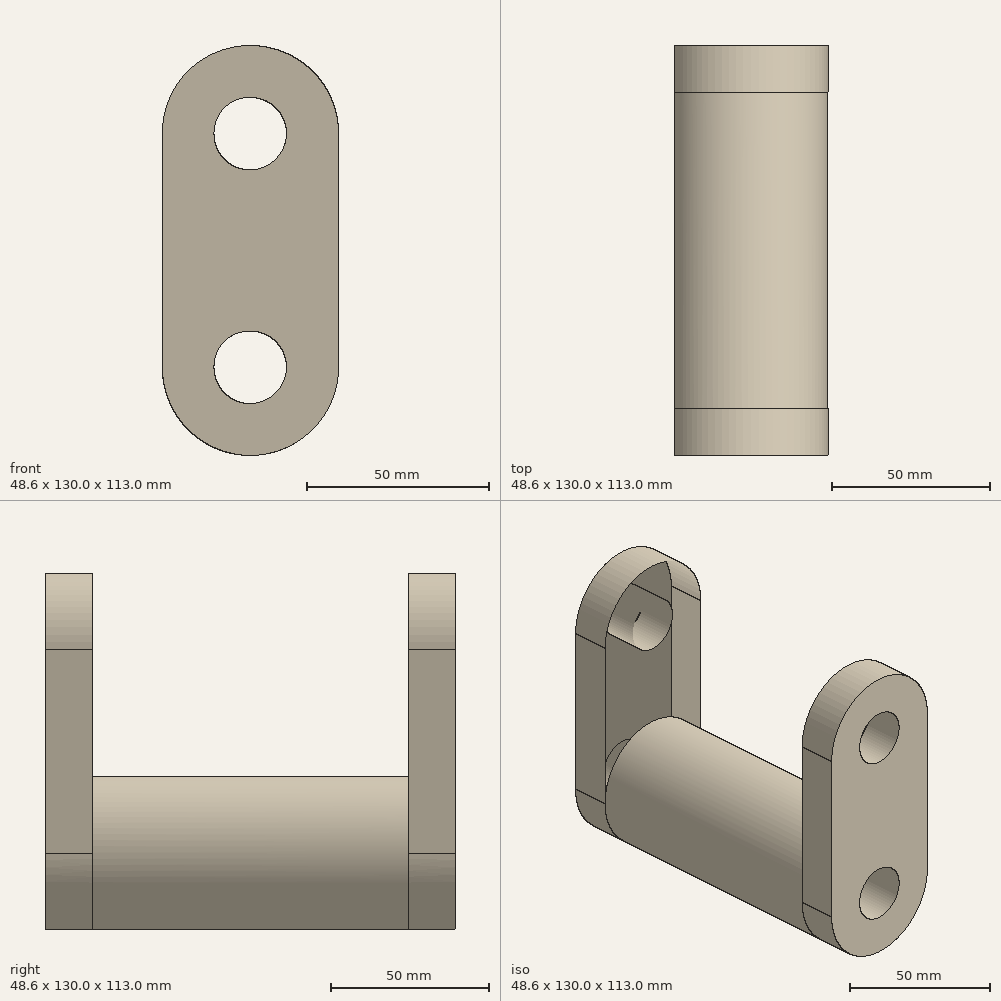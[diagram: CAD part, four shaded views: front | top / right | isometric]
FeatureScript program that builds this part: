
annotation { "Feature Type Name" : "Feature", "Feature Type Description" : "" }
export const myFeature = defineFeature(function(context is Context, id is Id, definition is map)
    precondition{}
    {
        {
            var Q0;
            Q0=qCreatedBy(makeId("Front.planeOp"),FACE);
            var sketch = newSketch(context, id + "F0", { "sketchPlane" : qUnion([Q0])});
            skCircle(sketch, "E0", {"center": v(0, -24.59) * mm, "radius": 24.22 * mm});
            skSolve(sketch);
        }
        {
            var Q0;
            Q0=makeQuery(id+"F0.imprint","IMPRINT",FACE,{"disambiguationData":[TD([[makeQuery(id+"F0.imprint","IMPRINT",EDGE,{"derivedFrom":sQuery(id+"F0.wireOp",EDGE,"E0")}),1.0]])]});
            extrude(context, id + "F1", {"entities" : qUnion([Q0]), "depth" : 50 * mm, "offsetDistance" : 25 * mm});
        }
        {
            var Q0;
            Q0=makeQuery(id+"F1.opExtrude","CAP_FACE",FACE,{"disambiguationData":[OSD([sQuery(id+"F0.wireOp",EDGE,"E0")])],"isStart":false});
            var sketch = newSketch(context, id + "F2", { "sketchPlane" : qUnion([Q0])});
            skPoint(sketch, "E1", {"position": v(0, -24.59) * mm});
            skLineSegment(sketch, "E2.bottom", {"start": v(-24.22, -24.59) * mm, "end": v(24.37, -24.59) * mm});
            skLineSegment(sketch, "E2.top", {"start": v(-24.22, 39.79) * mm, "end": v(24.37, 39.79) * mm});
            skLineSegment(sketch, "E2.left", {"start": v(-24.22, -24.59) * mm, "end": v(-24.22, 39.79) * mm});
            skLineSegment(sketch, "E2.right", {"start": v(24.37, -24.59) * mm, "end": v(24.37, 39.79) * mm});
            skArc(sketch, "E3", {"start": v(-24.22, -24.59) * mm, "mid": v(0.07, -48.88) * mm, "end": v(24.37, -24.59) * mm});
            skArc(sketch, "E4", {"start": v(24.37, 39.79) * mm, "mid": v(0.07, 64.08) * mm, "end": v(-24.22, 39.79) * mm});
            skSolve(sketch);
        }
        {
            var Q0;
            Q0 = qSketchRegion(id + "F2", true);
            extrude(context, id + "F3", {"entities" : qUnion([Q0]), "operationType" : NewBodyOperationType.ADD, "depth" : 15 * mm, "offsetDistance" : 25 * mm});
        }
        {
            var Q0;
            Q0=makeQuery(id+"F1.opExtrude","SWEPT_BODY",BODY,{"disambiguationData":[OSD([sQuery(id+"F0.wireOp",EDGE,"E0")])]});
            var Q1;
            Q1=qCreatedBy(makeId("Front.planeOp"),FACE);
            mirror(context, id + "F4", {"operationType" : NewBodyOperationType.ADD, "entities" : qUnion([Q0]), "mirrorPlane" : qUnion([Q1])});
        }
        {
            var Q0;
            Q0=makeQuery(id+"F3.opExtrude","CAP_FACE",FACE,{"disambiguationData":[OSD([sQuery(id+"F2.wireOp",EDGE,"E2.left"),sQuery(id+"F2.wireOp",EDGE,"E2.right"),sQuery(id+"F2.wireOp",EDGE,"E3"),sQuery(id+"F2.wireOp",EDGE,"E4")])],"isStart":false});
            var sketch = newSketch(context, id + "F5", { "sketchPlane" : qUnion([Q0])});
            skPoint(sketch, "E5", {"position": v(0, 39.79) * mm});
            skPoint(sketch, "E6", {"position": v(0, -24.59) * mm});
            skSolve(sketch);
        }
        {
            var Q0;
            Q0=sQuery(id+"F5.wireOp",VERTEX,"E5");
            var Q1;
            Q1=sQuery(id+"F5.wireOp",VERTEX,"E6");
            var Q2;
            Q2=makeQuery(id+"F1.opExtrude","SWEPT_BODY",BODY,{"disambiguationData":[OSD([sQuery(id+"F0.wireOp",EDGE,"E0")])]});
            hole(context, id + "F6", {"style" : HoleStyle.SIMPLE, "endStyle" : HoleEndStyle.THROUGH, "holeDiameter" : 20 * mm, "majorDiameter" : 5 * mm, "isTappedThrough" : true, "tappedDepth" : 12 * mm, "tapClearance" : 3, "locations" : qUnion([Q0, Q1]), "scope" : qUnion([Q2])});
        }
    });
